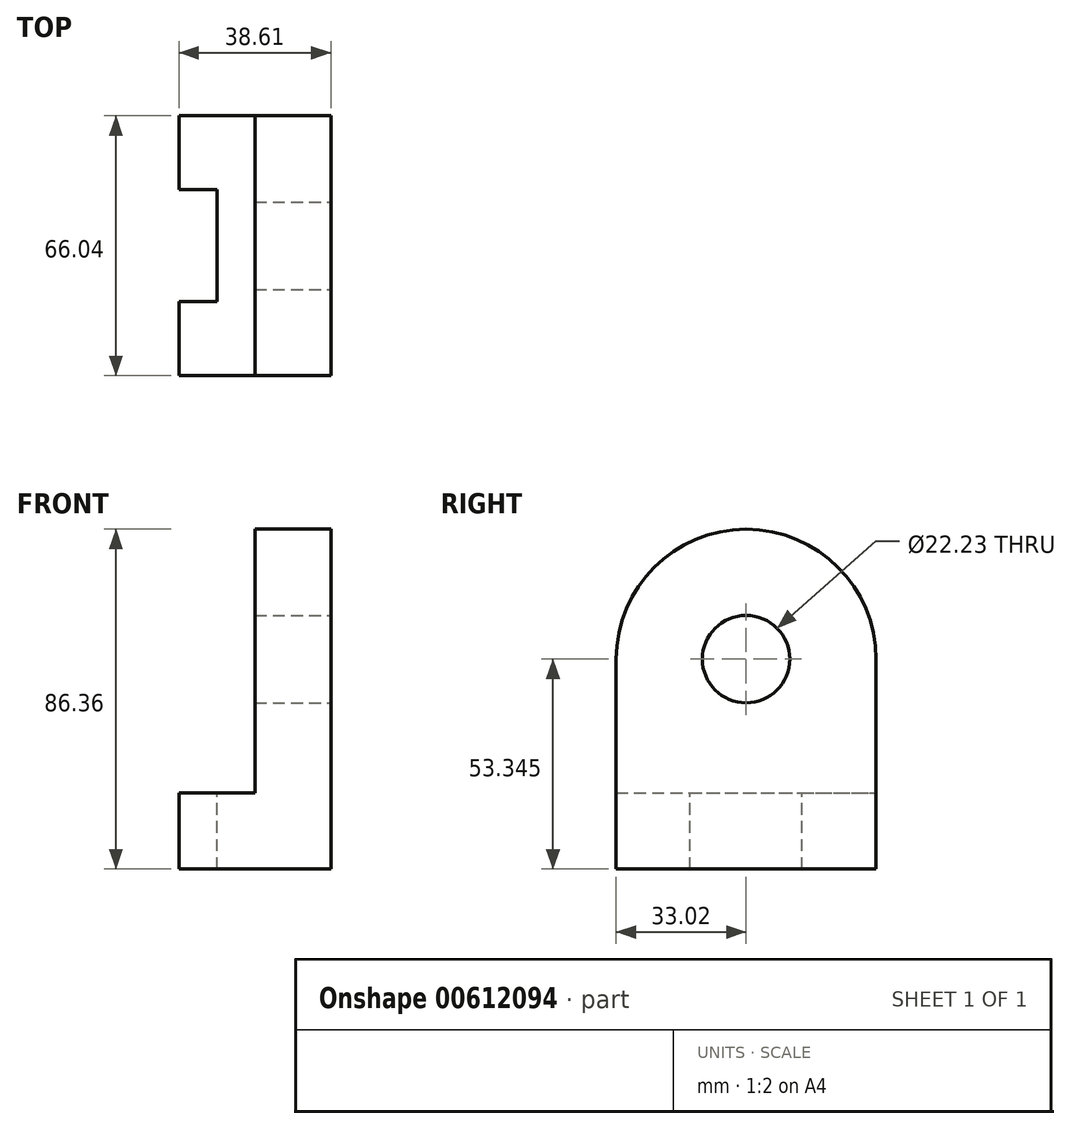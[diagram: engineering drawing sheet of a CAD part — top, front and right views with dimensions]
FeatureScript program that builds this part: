
annotation { "Feature Type Name" : "Feature", "Feature Type Description" : "" }
export const myFeature = defineFeature(function(context is Context, id is Id, definition is map)
    precondition{}
    {
        {
            var Q0;
            Q0=qCreatedBy(makeId("Front.planeOp"),FACE);
            var sketch = newSketch(context, id + "F0", { "sketchPlane" : qUnion([Q0])});
            skLineSegment(sketch, "E0", {"start": v(4.03, 41.02) * mm, "end": v(23.34, 41.02) * mm});
            skLineSegment(sketch, "E1", {"start": v(23.34, 41.02) * mm, "end": v(23.34, -45.34) * mm});
            skLineSegment(sketch, "E2", {"start": v(23.34, -45.34) * mm, "end": v(-15.27, -45.34) * mm});
            skLineSegment(sketch, "E3", {"start": v(-15.27, -45.34) * mm, "end": v(-15.27, -26.03) * mm});
            skLineSegment(sketch, "E4", {"start": v(-15.27, -26.03) * mm, "end": v(4.03, -26.03) * mm});
            skLineSegment(sketch, "E5", {"start": v(4.03, -26.03) * mm, "end": v(4.03, 41.02) * mm});
            skSolve(sketch);
        }
        {
            var Q0;
            Q0=makeQuery(id+"F0.imprint","IMPRINT",FACE,{"disambiguationData":[TD([[makeQuery(id+"F0.imprint","IMPRINT",EDGE,{"derivedFrom":sQuery(id+"F0.wireOp",EDGE,"E0")}),-1.0]])]});
            extrude(context, id + "F1", {"entities" : qUnion([Q0]), "depth" : 66.04 * mm, "offsetDistance" : 25.4 * mm});
        }
        {
            var Q0;
            Q0=makeQuery(id+"F1.opExtrude","CAP_EDGE",EDGE,{"disambiguationData":[OSD([sQuery(id+"F0.wireOp",EDGE,"E0")])],"isStart":true});
            fillet(context, id + "F2", {"entities" : qUnion([Q0]), "radius" : 33.02 * mm, "tangentPropagation" : true, "allowEdgeOverflow" : false});
        }
        {
            var Q0;
            Q0=makeQuery(id+"F1.opExtrude","CAP_EDGE",EDGE,{"disambiguationData":[OSD([sQuery(id+"F0.wireOp",EDGE,"E0")])],"isStart":false});
            fillet(context, id + "F3", {"entities" : qUnion([Q0]), "radius" : 33.02 * mm, "tangentPropagation" : true, "allowEdgeOverflow" : false});
        }
        {
            var Q0;
            Q0=makeQuery(id+"F1.opExtrude","SWEPT_FACE",FACE,{"disambiguationData":[OSD([sQuery(id+"F0.wireOp",EDGE,"E3")])]});
            var sketch = newSketch(context, id + "F4", { "sketchPlane" : qUnion([Q0])});
            skLineSegment(sketch, "E6.top", {"start": v(18.8, -45.34) * mm, "end": v(47.24, -45.34) * mm});
            skLineSegment(sketch, "E7", {"start": v(0, -45.34) * mm, "end": v(66.04, -45.34) * mm});
            skLineSegment(sketch, "E8", {"start": v(66.04, -26.03) * mm, "end": v(66.04, 8) * mm});
            skLineSegment(sketch, "E9", {"start": v(66.04, 8) * mm, "end": v(0, 8) * mm});
            skLineSegment(sketch, "E10", {"start": v(0, 8) * mm, "end": v(0, -26.03) * mm});
            skArc(sketch, "E11", {"start": v(0, 8) * mm, "mid": v(33.02, 41.02) * mm, "end": v(66.04, 8) * mm});
            skCircle(sketch, "E12", {"center": v(33.02, 8) * mm, "radius": 11.11 * mm});
            skLineSegment(sketch, "E13", {"start": v(18.8, -45.34) * mm, "end": v(0, -45.34) * mm});
            skLineSegment(sketch, "E14", {"start": v(18.8, -45.34) * mm, "end": v(18.8, -26.03) * mm});
            skLineSegment(sketch, "E15", {"start": v(47.24, -45.34) * mm, "end": v(47.24, -26.03) * mm});
            skSolve(sketch);
        }
        {
            var Q0;
            {var subQ0=sQuery(id+"F4.wireOp",EDGE,"E14");Q0=makeQuery(id+"F4.imprint","IMPRINT",FACE,{"disambiguationData":[TD([[makeQuery(id+"F4.imprint","IMPRINT",EDGE,{"derivedFrom":subQ0}),-1.0]])]});}
            extrude(context, id + "F5", {"entities" : qUnion([Q0]), "operationType" : NewBodyOperationType.REMOVE, "oppositeDirection" : true, "depth" : 9.65 * mm, "offsetDistance" : 25.4 * mm});
        }
        {
            var Q0;
            Q0=makeQuery(id+"F1.opExtrude","SWEPT_FACE",FACE,{"disambiguationData":[OSD([sQuery(id+"F0.wireOp",EDGE,"E1")])]});
            var sketch = newSketch(context, id + "F6", { "sketchPlane" : qUnion([Q0])});
            skCircle(sketch, "E16", {"center": v(-33.02, 8) * mm, "radius": 11.11 * mm});
            skSolve(sketch);
        }
        {
            var Q0;
            Q0=makeQuery(id+"F6.imprint","IMPRINT",FACE,{"disambiguationData":[TD([[makeQuery(id+"F6.imprint","IMPRINT",EDGE,{"derivedFrom":sQuery(id+"F6.wireOp",EDGE,"E16")}),1.0]])]});
            extrude(context, id + "F7", {"entities" : qUnion([Q0]), "operationType" : NewBodyOperationType.REMOVE, "oppositeDirection" : true, "depth" : 19.3 * mm, "offsetDistance" : 25.4 * mm});
        }
    });
